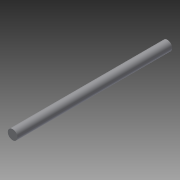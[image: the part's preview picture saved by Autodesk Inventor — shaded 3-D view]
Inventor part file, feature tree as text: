
AUTODESK INVENTOR PART (.ipt)
format: ipt  version: 2015 SP1 (Build 190203100, 203)  size: 98,816 bytes
history: native  units: in
note: dims shown in document units (in); Inventor stores cm internally (conversion verified against a paired STEP export)
features: sketch x2, sweep x1
ambient origin geometry x8: Origin, YZ Plane, XZ Plane, XY Plane, X Axis, Y Axis, Z Axis, Center Point
bodies: Body1 (feature_tree)
feature tree (3):
  sweep  "Sweep1"
  sketch  "Sketch2"  dims[d3=4.0in d4=90.0deg]
  sketch  "Sketch3"  dims[d5=0.5in d6=1.0in d7=1.0in d8=0.5in d9=0.5in d10=0.5in d11=0.25in d12=0.0in d13=0.0in]
